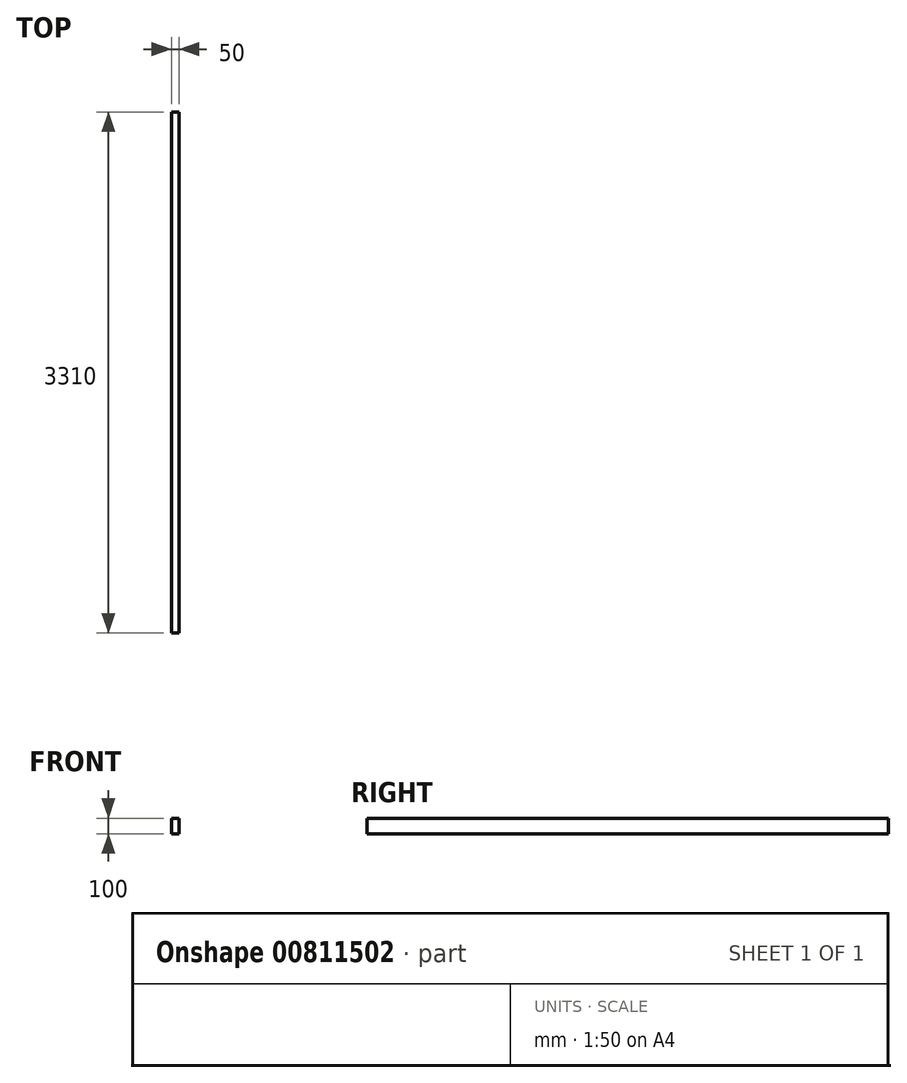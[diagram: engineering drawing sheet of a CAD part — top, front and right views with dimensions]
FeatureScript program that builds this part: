
annotation { "Feature Type Name" : "Feature", "Feature Type Description" : "" }
export const myFeature = defineFeature(function(context is Context, id is Id, definition is map)
    precondition{}
    {
        {
            var Q0;
            Q0=qCreatedBy(makeId("Front.planeOp"),FACE);
            var sketch = newSketch(context, id + "F0", { "sketchPlane" : qUnion([Q0])});
            skLineSegment(sketch, "E0.bottom", {"start": v(25, 50) * mm, "end": v(-25, 50) * mm});
            skLineSegment(sketch, "E0.top", {"start": v(25, -50) * mm, "end": v(-25, -50) * mm});
            skLineSegment(sketch, "E0.left", {"start": v(25, 50) * mm, "end": v(25, -50) * mm});
            skLineSegment(sketch, "E0.right", {"start": v(-25, 50) * mm, "end": v(-25, -50) * mm});
            skPoint(sketch, "E0.middle", {"position": v(0, 0) * mm});
            skSolve(sketch);
        }
        {
            var Q0;
            Q0=makeQuery(id+"F0.imprint","IMPRINT",FACE,{"disambiguationData":[TD([[makeQuery(id+"F0.imprint","IMPRINT",EDGE,{"derivedFrom":sQuery(id+"F0.wireOp",EDGE,"E0.bottom")}),1.0]])]});
            extrude(context, id + "F1", {"entities" : qUnion([Q0]), "endBound" : BoundingType.SYMMETRIC, "depth" : 3310 * mm, "offsetDistance" : 25.4 * mm});
        }
    });
